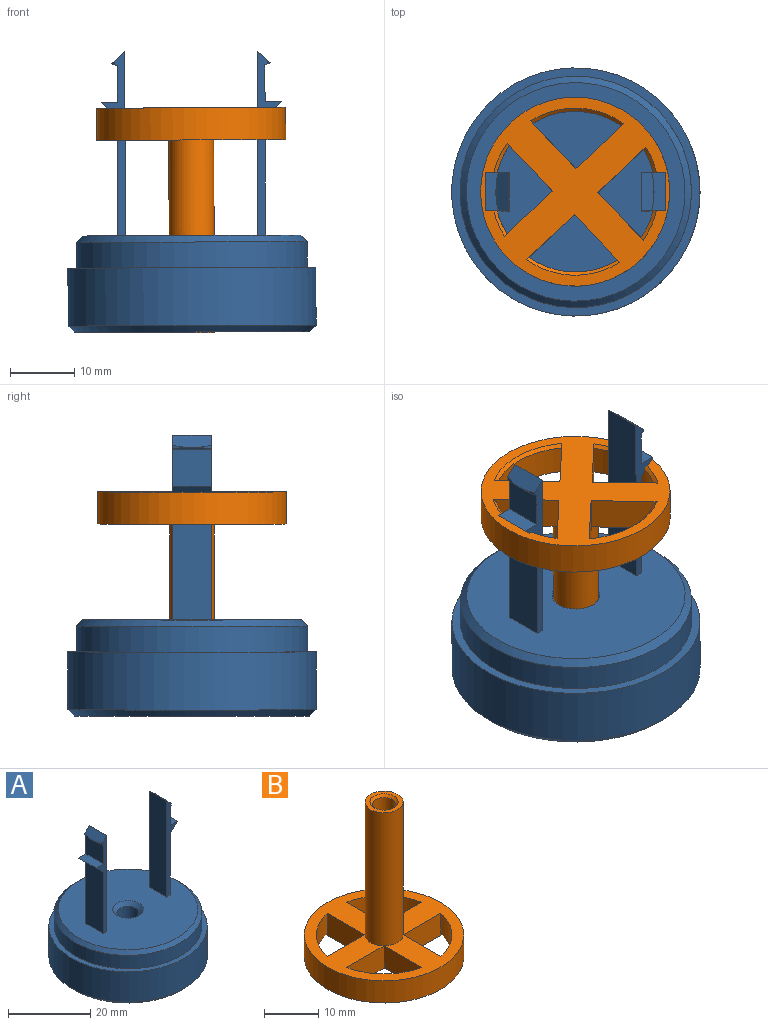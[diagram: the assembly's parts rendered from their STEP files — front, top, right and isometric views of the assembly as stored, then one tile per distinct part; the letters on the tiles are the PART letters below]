
ASSEMBLY  parts=2 mates=1
PART A: 32 faces, bbox 38.6x38.6x43.7 mm
  f0: plane 6x2.5mm, normal (0,0,1), area 15mm2, adj f1,f2,f3,f12
  f1: plane 28.66x3.7mm, normal (0,-1,0), area 37.2mm2, adj f0,f3,f4,f10,f11,f12,f13,f14
  f2: plane 28.66x3.7mm, normal (0,1,0), area 37.2mm2, adj f0,f3,f4,f10,f11,f12,f13,f14
  f3: plane 6x2.5mm, normal (-0.71,0,-0.71), area 21.2mm2, adj f0,f1,f2,f4
  f4: plane 18.3x6mm, normal (-1,0,0), area 109.8mm2, adj f1,f2,f3,f15
  f5: plane 6x2.5mm, normal (0,0,1), area 15mm2, adj f6,f7,f8,f18
  f6: plane 28.66x3.7mm, normal (0,-1,0), area 37.2mm2, adj f5,f8,f9,f15,f16,f17,f18,f19
  f7: plane 28.66x3.7mm, normal (0,1,0), area 37.2mm2, adj f5,f8,f9,f15,f16,f17,f18,f19
  f8: plane 6x2.5mm, normal (0.71,0,-0.71), area 21.2mm2, adj f5,f6,f7,f9
  f9: plane 18.3x6mm, normal (1,0,0), area 109.8mm2, adj f6,f7,f8,f15
  f10: plane 6x2mm, normal (-0.68,0,0.73), area 15.4mm2, adj f1,f2,f13,f14
  f11: plane 6x0.8mm, normal (-0.35,0,-0.94), area 4.3mm2, adj f1,f2,f12,f14
  f12: plane 6x5.7mm, normal (-1,0,0), area 34.2mm2, adj f0,f1,f2,f11
  f13: plane 28.66x6mm, normal (1,0,0), area 171.9mm2, adj f1,f2,f10,f15
  f14: cylinder r=12.3mm len=6mm, axis (0,0,-1), area 1mm2, adj f1,f2,f10,f11
  f15: plane 34x34mm, normal (0,0,1), area 850.5mm2, adj f1,f2,f4,f6,f7,f9,f13,f19
  f16: plane 6x0.8mm, normal (0.35,0,-0.94), area 4.3mm2, adj f6,f7,f18,f20
  f17: plane 6x2mm, normal (0.68,0,0.73), area 15.4mm2, adj f6,f7,f19,f20
  f18: plane 6x5.7mm, normal (1,0,0), area 34.2mm2, adj f5,f6,f7,f16
  f19: plane 28.66x6mm, normal (-1,0,0), area 171.9mm2, adj f6,f7,f15,f17
  f20: cylinder r=12.3mm len=6mm, axis (0,0,-1), area 1mm2, adj f6,f7,f16,f17
  f21: cylinder r=3.75mm len=9mm, axis (0,0,1), area 212.1mm2, adj f27,f29
  f22: cylinder r=19.3mm len=38.6mm, axis (0,0,1), area 1091.4mm2, adj f24,f28
  f23: plane 36.6x36.6mm, normal (0,0,-1), area 981.2mm2, adj f28,f29
  f24: plane 38.6x38.6mm, normal (0,0,1), area 152.3mm2, adj f22,f26
  f25: cylinder r=2.7mm len=5.4mm, axis (0,0,1), area 67.9mm2, adj f27,f31
  f26: cylinder r=18mm len=36mm, axis (0,0,1), area 452.4mm2, adj f24,f30
  f27: plane 7.5x7.5mm, normal (0,0,-1), area 21.3mm2, adj f21,f25
  f28: cone r=19.3mm half-angle=45deg, axis (0,0,1), area 167.1mm2, adj f22,f23
  f29: cone r=4.75mm half-angle=45deg, axis (0,0,-1), area 37.8mm2, adj f21,f23
  f30: cone r=17mm half-angle=45deg, axis (0,0,-1), area 155.5mm2, adj f15,f26
  f31: cone r=2.7mm half-angle=45deg, axis (0,0,1), area 28.4mm2, adj f15,f25
PART B: 24 faces, bbox 29.4x29.4x35 mm
  f0: cylinder r=12.5mm len=9.75mm, axis (0,0,-1), area 65.7mm2, adj f1,f12,f13,f19
  f1: plane 10.26x5mm, normal (0,-1,0), area 48.9mm2, adj f0,f12,f13,f14,f19
  f2: plane 10.26x5mm, normal (1,0,0), area 48.9mm2, adj f3,f8,f13,f14,f20
  f3: cylinder r=12.5mm len=9.75mm, axis (0,0,-1), area 65.7mm2, adj f2,f8,f13,f20
  f4: cylinder r=12.5mm len=9.75mm, axis (0,0,-1), area 65.7mm2, adj f5,f9,f13,f21
  f5: plane 10.26x5mm, normal (1,0,0), area 48.9mm2, adj f4,f9,f13,f14,f21
  f6: cylinder r=12.5mm len=9.75mm, axis (0,0,-1), area 65.7mm2, adj f7,f10,f13,f22
  f7: plane 10.26x5mm, normal (-1,0,0), area 48.9mm2, adj f6,f10,f13,f14,f22
  f8: plane 10.26x5mm, normal (0,1,0), area 48.9mm2, adj f2,f3,f13,f14,f20
  f9: plane 10.26x5mm, normal (0,-1,0), area 48.9mm2, adj f4,f5,f13,f14,f21
  f10: plane 10.26x5mm, normal (0,1,0), area 48.9mm2, adj f6,f7,f13,f14,f22
  f11: cylinder r=14.7mm len=29.4mm, axis (0,0,-1), area 461.8mm2, adj f13,f14
  f12: plane 10.26x5mm, normal (-1,0,0), area 48.9mm2, adj f0,f1,f13,f14,f19
  f13: plane 29.4x29.4mm, normal (0,0,1), area 372.8mm2, adj f0,f1,f2,f3,f4,f5,f6,f7
  f14: plane 29.4x29.4mm, normal (0,0,-1), area 381.3mm2, adj f1,f2,f5,f7,f8,f9,f10,f11
  f15: cylinder r=3.5mm len=30mm, axis (0,0,-1), area 659.7mm2, adj f13,f16
  f16: plane 7x7mm, normal (0,0,1), area 17.2mm2, adj f15,f23
  f17: cylinder r=2.1mm len=21.5mm, axis (0,0,1), area 283.7mm2, adj f18,f23
  f18: plane 4.2x4.2mm, normal (0,0,1), area 13.9mm2, adj f17
  f19: cone r=13mm half-angle=45deg, axis (0,0,-1), area 10.6mm2, adj f0,f1,f12,f14
  f20: cone r=13mm half-angle=45deg, axis (0,0,-1), area 10.6mm2, adj f2,f3,f8,f14
  f21: cone r=13mm half-angle=45deg, axis (0,0,-1), area 10.6mm2, adj f4,f5,f9,f14
  f22: cone r=13mm half-angle=45deg, axis (0,0,-1), area 10.6mm2, adj f6,f7,f10,f14
  f23: cone r=2.1mm half-angle=45deg, axis (0,0,1), area 10.4mm2, adj f16,f17
PLACE A rot(axis=(0,-1,0),0.2deg) t=(-0.17,0.12,1.25)mm fixed
PLACE B rot(axis=(-0.37,0.93,0),179.8deg) t=(-0.25,0.12,21.12)mm
MATE cylindrical A.f26 <-> B.f15  axis (0,0,1) through (-0.17,0.12,1.25)mm
